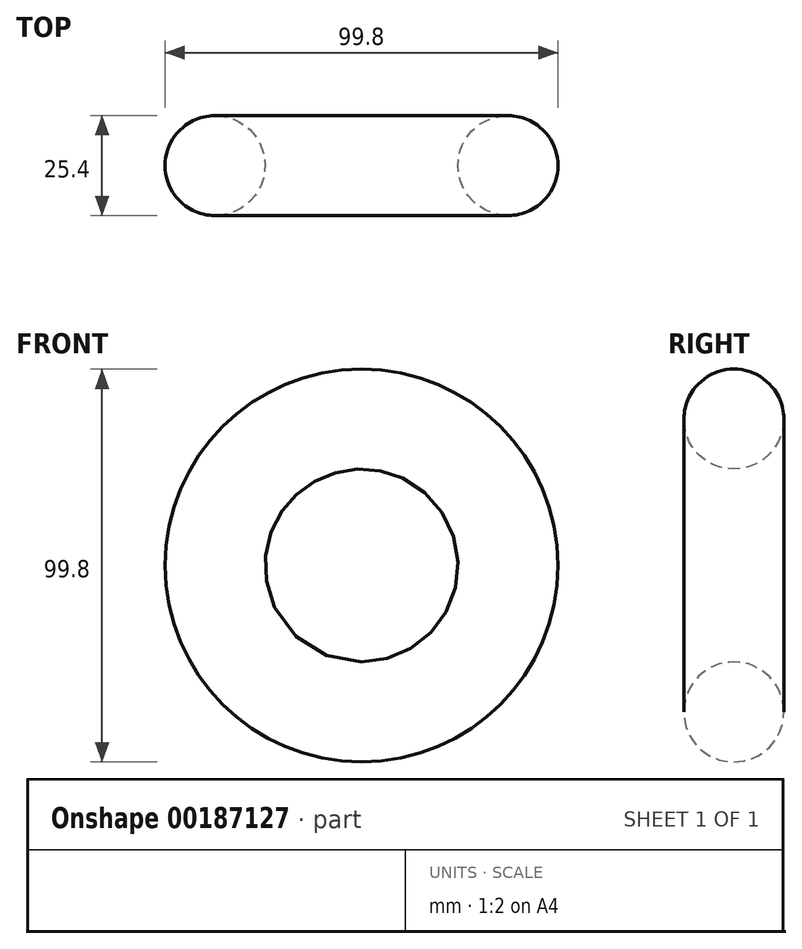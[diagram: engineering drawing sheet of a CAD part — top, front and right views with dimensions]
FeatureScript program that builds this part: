
annotation { "Feature Type Name" : "Feature", "Feature Type Description" : "" }
export const myFeature = defineFeature(function(context is Context, id is Id, definition is map)
    precondition{}
    {
        {
            var Q0;
            Q0=qCreatedBy(makeId("Right.planeOp"),FACE);
            var sketch = newSketch(context, id + "F0", { "sketchPlane" : qUnion([Q0])});
            skCircle(sketch, "E0", {"center": v(0, 37.2) * mm, "radius": 12.7 * mm});
            skSolve(sketch);
        }
        {
            var Q0;
            Q0=qCreatedBy(makeId("Right.planeOp"),FACE);
            var sketch = newSketch(context, id + "F1", { "sketchPlane" : qUnion([Q0])});
            skLineSegment(sketch, "E1", {"start": v(-18.01, 0) * mm, "end": v(18.47, 0) * mm});
            skSolve(sketch);
        }
        {
            var Q0;
            Q0=makeQuery(id+"F0.imprint","IMPRINT",FACE,{"disambiguationData":[TD([[makeQuery(id+"F0.imprint","IMPRINT",EDGE,{"derivedFrom":sQuery(id+"F0.wireOp",EDGE,"E0")}),1.0]])]});
            var Q1;
            Q1=sQuery(id+"F1.wireOp",EDGE,"E1");
            revolve(context, id + "F2", {"entities" : qUnion([Q0]), "axis" : qUnion([Q1]), "revolveType" : RevolveType.FULL});
        }
    });
